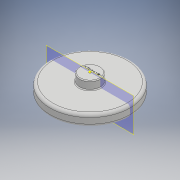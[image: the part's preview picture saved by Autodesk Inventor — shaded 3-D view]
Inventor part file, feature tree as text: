
AUTODESK INVENTOR PART (.ipt)
format: ipt  version: 2018 (Build 220112000, 112)  size: 182,784 bytes
history: native  units: mm
features: sketch x9, extrude x5, fillet x4, other x1, hole x1
ambient origin geometry x8: Origin, YZ Plane, XZ Plane, XY Plane, X Axis, Y Axis, Z Axis, Center Point
bodies: Body1 (feature_tree)
feature tree (20):
  other  "ソリッド1"
  extrude  "押し出し1"  Depth=490.0mm
  fillet  "フィレット1"  Radius=70.0mm
  sketch  "スケッチ4"
  extrude  "押し出し2"  Depth=17.5mm
  extrude  "押し出し3"  Depth=128.0mm
  fillet  "フィレット2"  Radius=50.0mm
  fillet  "フィレット3"  Radius=216.0mm
  fillet  "フィレット4"  Radius=48.0mm
  hole  "穴2"  [1 undecoded]
  sketch  "スケッチ12"
  sketch  "スケッチ13"
  sketch  "スケッチ14"
  sketch  "スケッチ15"
  extrude  "押し出し4"  Depth=5.0mm
  extrude  "押し出し5"  Depth=5.0mm
  sketch  "スケッチ1"
  sketch  "スケッチ8"
  sketch  "スケッチ9"
  sketch  "スケッチ10"
note: 1 required parameter value undecoded (feature->parameter linkage not recoverable at this tier; creation-order binding heuristic only, values carry confidence <= 0.55)
